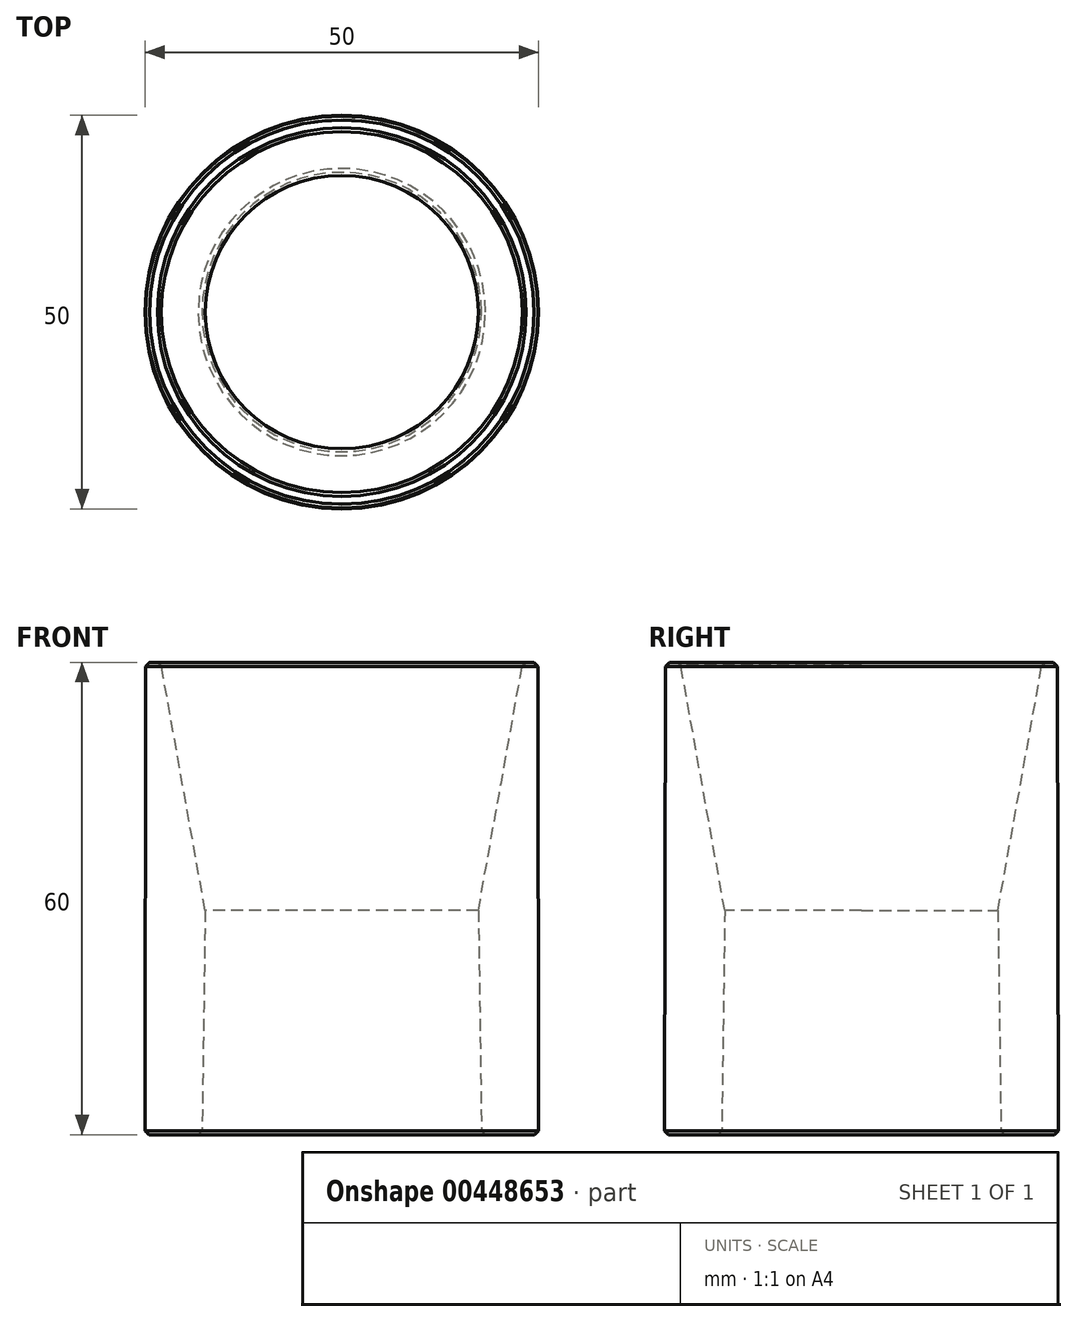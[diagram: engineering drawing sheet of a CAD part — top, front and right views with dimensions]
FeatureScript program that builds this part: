
annotation { "Feature Type Name" : "Feature", "Feature Type Description" : "" }
export const myFeature = defineFeature(function(context is Context, id is Id, definition is map)
    precondition{}
    {
        {
            var Q0;
            Q0=qCreatedBy(makeId("Front.planeOp"),FACE);
            var sketch = newSketch(context, id + "F0", { "sketchPlane" : qUnion([Q0])});
            skLineSegment(sketch, "E0.bottom", {"start": v(-24.9, 30) * mm, "end": v(24.9, 30) * mm});
            skLineSegment(sketch, "E0.top", {"start": v(-25, -30) * mm, "end": v(25, -30) * mm});
            skLineSegment(sketch, "E0.right", {"start": v(24.9, 30) * mm, "end": v(25, -30) * mm});
            skLineSegment(sketch, "E1", {"start": v(-23, 30) * mm, "end": v(-17.35, -1.5) * mm});
            skLineSegment(sketch, "E2", {"start": v(-17.35, -1.5) * mm, "end": v(-17.75, -30) * mm});
            skLineSegment(sketch, "E3.MirrorCS", {"start": v(17.35, -1.5) * mm, "end": v(17.75, -30) * mm});
            skLineSegment(sketch, "E4.MirrorCS", {"start": v(23, 30) * mm, "end": v(17.35, -1.5) * mm});
            skLineSegment(sketch, "E5", {"start": v(0, 32.4) * mm, "end": v(0, -30.04) * mm, "construction": true});
            skPoint(sketch, "E5.endSnap0", {"position": v(0, -30) * mm});
            skLineSegment(sketch, "E6", {"start": v(-25, -30) * mm, "end": v(-24.9, 30) * mm});
            skSolve(sketch);
        }
        {
            var Q0;
            {var subQ0=sQuery(id+"F0.wireOp",EDGE,"E1");Q0=makeQuery(id+"F0.imprint","IMPRINT",FACE,{"disambiguationData":[TD([[makeQuery(id+"F0.imprint","IMPRINT",EDGE,{"derivedFrom":subQ0}),-1.0]])]});}
            var Q1;
            Q1=sQuery(id+"F0.wireOp",EDGE,"E5");
            revolve(context, id + "F1", {"entities" : qUnion([Q0]), "axis" : qUnion([Q1]), "revolveType" : RevolveType.FULL});
        }
        {
            var Q0;
            Q0=makeQuery(id+"F1.opRevolve","SWEPT_EDGE",EDGE,{"disambiguationData":[OSD([sQuery(id+"F0.wireOp",EDGE,"E0.bottom"),sQuery(id+"F0.wireOp",EDGE,"E1")])]});
            var Q1;
            Q1=makeQuery(id+"F1.opRevolve","SWEPT_EDGE",EDGE,{"disambiguationData":[OSD([sQuery(id+"F0.wireOp",EDGE,"E0.bottom"),sQuery(id+"F0.wireOp",EDGE,"E6")])]});
            var Q2;
            Q2=makeQuery(id+"F1.opRevolve","SWEPT_EDGE",EDGE,{"disambiguationData":[OSD([sQuery(id+"F0.wireOp",EDGE,"E0.top"),sQuery(id+"F0.wireOp",EDGE,"E6")])]});
            var Q3;
            Q3=makeQuery(id+"F1.opRevolve","SWEPT_EDGE",EDGE,{"disambiguationData":[OSD([sQuery(id+"F0.wireOp",EDGE,"E0.top"),sQuery(id+"F0.wireOp",EDGE,"E2")])]});
            chamfer(context, id + "F2", {"entities" : qUnion([Q0, Q1, Q2, Q3]), "width" : .5 * mm, "tangentPropagation" : true});
        }
    });
